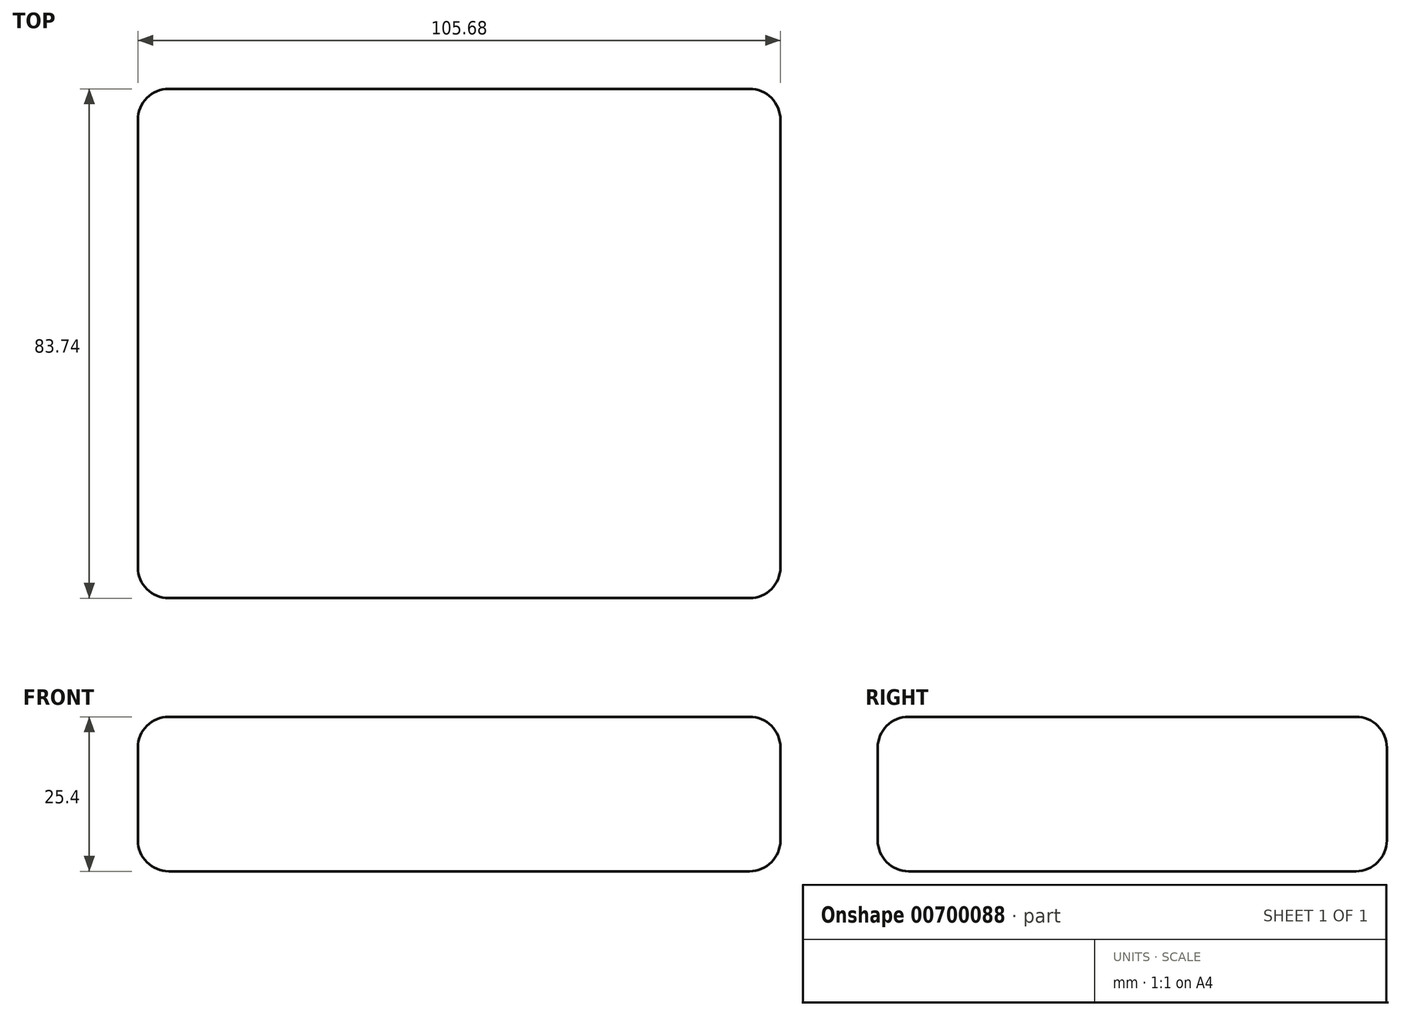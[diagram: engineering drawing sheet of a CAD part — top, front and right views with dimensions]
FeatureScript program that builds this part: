
annotation { "Feature Type Name" : "Feature", "Feature Type Description" : "" }
export const myFeature = defineFeature(function(context is Context, id is Id, definition is map)
    precondition{}
    {
        {
            var Q0;
            Q0=qCreatedBy(makeId("Top.planeOp"),FACE);
            var sketch = newSketch(context, id + "F0", { "sketchPlane" : qUnion([Q0])});
            skLineSegment(sketch, "E0.bottom", {"start": v(-50.34, 45.87) * mm, "end": v(55.34, 45.87) * mm});
            skLineSegment(sketch, "E0.top", {"start": v(-50.34, -37.87) * mm, "end": v(55.34, -37.87) * mm});
            skLineSegment(sketch, "E0.left", {"start": v(-50.34, 45.87) * mm, "end": v(-50.34, -37.87) * mm});
            skLineSegment(sketch, "E0.right", {"start": v(55.34, 45.87) * mm, "end": v(55.34, -37.87) * mm});
            skSolve(sketch);
        }
        {
            var Q0;
            Q0 = qSketchRegion(id + "F0", true);
            extrude(context, id + "F1", {"entities" : qUnion([Q0]), "depth" : 25.4 * mm, "offsetDistance" : 25.4 * mm});
        }
        {
            var Q0;
            Q0=makeQuery(id+"F1.opExtrude","CAP_FACE",FACE,{"disambiguationData":[OSD([sQuery(id+"F0.wireOp",EDGE,"E0.bottom"),sQuery(id+"F0.wireOp",EDGE,"E0.top"),sQuery(id+"F0.wireOp",EDGE,"E0.left"),sQuery(id+"F0.wireOp",EDGE,"E0.right")])],"isStart":true});
            var Q1;
            Q1=makeQuery(id+"F1.opExtrude","SWEPT_FACE",FACE,{"disambiguationData":[OSD([sQuery(id+"F0.wireOp",EDGE,"E0.left")])]});
            var Q2;
            Q2=makeQuery(id+"F1.opExtrude","SWEPT_FACE",FACE,{"disambiguationData":[OSD([sQuery(id+"F0.wireOp",EDGE,"E0.bottom")])]});
            var Q3;
            Q3=makeQuery(id+"F1.opExtrude","CAP_EDGE",EDGE,{"disambiguationData":[OSD([sQuery(id+"F0.wireOp",EDGE,"E0.bottom")])],"isStart":true});
            var Q4;
            Q4=makeQuery(id+"F1.opExtrude","SWEPT_EDGE",EDGE,{"disambiguationData":[OSD([sQuery(id+"F0.wireOp",EDGE,"E0.bottom"),sQuery(id+"F0.wireOp",EDGE,"E0.right")])]});
            var Q5;
            Q5=makeQuery(id+"F1.opExtrude","CAP_EDGE",EDGE,{"disambiguationData":[OSD([sQuery(id+"F0.wireOp",EDGE,"E0.right")])],"isStart":false});
            var Q6;
            Q6=makeQuery(id+"F1.opExtrude","SWEPT_FACE",FACE,{"disambiguationData":[OSD([sQuery(id+"F0.wireOp",EDGE,"E0.right")])]});
            var Q7;
            Q7=makeQuery(id+"F1.opExtrude","SWEPT_FACE",FACE,{"disambiguationData":[OSD([sQuery(id+"F0.wireOp",EDGE,"E0.top")])]});
            fillet(context, id + "F2", {"entities" : qUnion([Q0, Q1, Q2, Q3, Q4, Q5, Q6, Q7]), "radius" : 5.08 * mm, "tangentPropagation" : true, "allowEdgeOverflow" : false});
        }
    });
